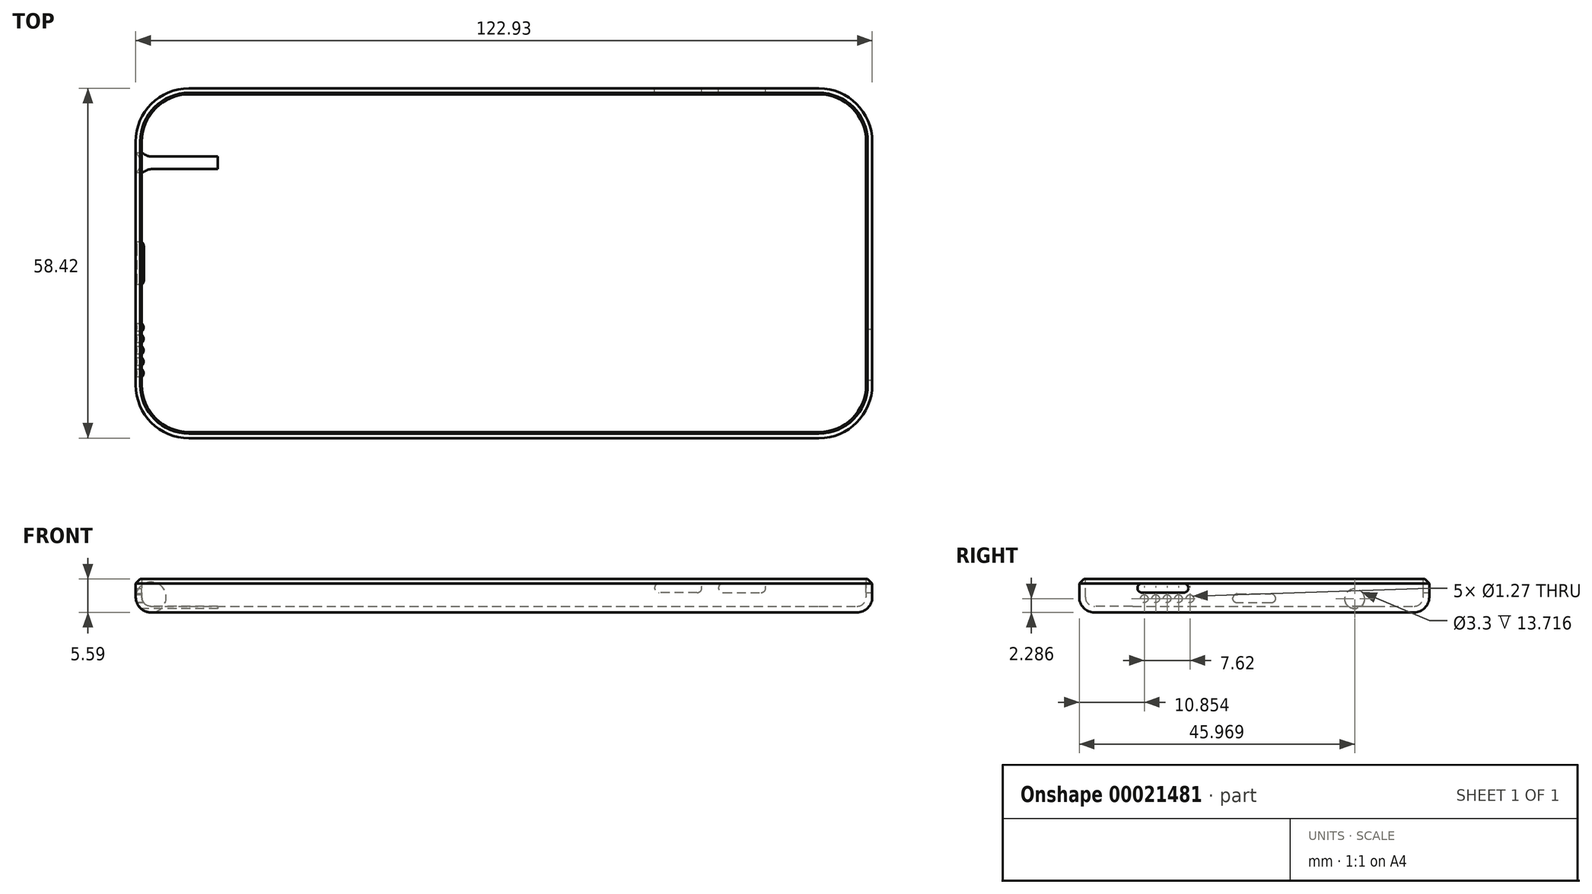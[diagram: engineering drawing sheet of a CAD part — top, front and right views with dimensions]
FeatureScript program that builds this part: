
annotation { "Feature Type Name" : "Feature", "Feature Type Description" : "" }
export const myFeature = defineFeature(function(context is Context, id is Id, definition is map)
    precondition{}
    {
        {
            var Q0;
            Q0=qCreatedBy(makeId("Top.planeOp"),FACE);
            var sketch = newSketch(context, id + "F0", { "sketchPlane" : qUnion([Q0])});
            skLineSegment(sketch, "E0.bottom", {"start": v(-46.61, 26.92) * mm, "end": v(58.54, 26.92) * mm});
            skLineSegment(sketch, "E0.top", {"start": v(-46.61, -31.5) * mm, "end": v(58.54, -31.5) * mm});
            skLineSegment(sketch, "E0.left", {"start": v(-55.5, 18.03) * mm, "end": v(-55.5, -22.61) * mm});
            skLineSegment(sketch, "E0.right", {"start": v(67.43, 18.03) * mm, "end": v(67.43, -22.61) * mm});
            skPoint(sketch, "E1.visualSharp", {"position": v(-55.5, 26.92) * mm});
            skArc(sketch, "E1.filletArc", {"start": v(-46.61, 26.92) * mm, "mid": v(-52.9, 24.31) * mm, "end": v(-55.5, 18.03) * mm});
            skPoint(sketch, "E2.visualSharp", {"position": v(67.43, 26.92) * mm});
            skArc(sketch, "E2.filletArc", {"start": v(67.43, 18.03) * mm, "mid": v(64.83, 24.31) * mm, "end": v(58.54, 26.92) * mm});
            skPoint(sketch, "E3.visualSharp", {"position": v(67.43, -31.5) * mm});
            skArc(sketch, "E3.filletArc", {"start": v(58.54, -31.5) * mm, "mid": v(64.83, -28.9) * mm, "end": v(67.43, -22.61) * mm});
            skPoint(sketch, "E4.visualSharp", {"position": v(-55.5, -31.5) * mm});
            skArc(sketch, "E4.filletArc", {"start": v(-55.5, -22.61) * mm, "mid": v(-52.9, -28.9) * mm, "end": v(-46.61, -31.5) * mm});
            skSolve(sketch);
        }
        {
            var Q0;
            Q0=makeQuery(id+"F0.imprint","IMPRINT",FACE,{"disambiguationData":[TD([[makeQuery(id+"F0.imprint","IMPRINT",EDGE,{"derivedFrom":sQuery(id+"F0.wireOp",EDGE,"E0.bottom")}),-1.0]])]});
            extrude(context, id + "F1", {"entities" : qUnion([Q0]), "depth" : 5.6 * mm});
        }
        {
            var Q0;
            Q0=makeQuery(id+"F1.opExtrude","SWEPT_FACE",FACE,{"disambiguationData":[OSD([sQuery(id+"F0.wireOp",EDGE,"E0.right")])]});
            var sketch = newSketch(context, id + "F2", { "sketchPlane" : qUnion([Q0])});
            skLineSegment(sketch, "E5", {"start": v(-14.04, 3.3) * mm, "end": v(-21.03, 3.3) * mm});
            skArc(sketch, "E6", {"start": v(-21.03, 4.83) * mm, "mid": v(-21.79, 4.06) * mm, "end": v(-21.03, 3.3) * mm});
            skArc(sketch, "E7", {"start": v(-14.04, 3.3) * mm, "mid": v(-13.28, 4.06) * mm, "end": v(-14.04, 4.83) * mm});
            skLineSegment(sketch, "E8", {"start": v(-14.04, 4.83) * mm, "end": v(-21.03, 4.83) * mm});
            skSolve(sketch);
        }
        {
            var Q0;
            Q0=makeQuery(id+"F1.opExtrude","SWEPT_FACE",FACE,{"disambiguationData":[OSD([sQuery(id+"F0.wireOp",EDGE,"E0.bottom")])]});
            var sketch = newSketch(context, id + "F3", { "sketchPlane" : qUnion([Q0])});
            skLineSegment(sketch, "E9", {"start": v(-42.54, 3.3) * mm, "end": v(-48.9, 3.3) * mm});
            skLineSegment(sketch, "E10", {"start": v(-49.65, 4.06) * mm, "end": v(-49.65, 4.06) * mm});
            skLineSegment(sketch, "E11", {"start": v(-48.9, 4.83) * mm, "end": v(-42.54, 4.83) * mm});
            skLineSegment(sketch, "E12", {"start": v(-41.78, 4.06) * mm, "end": v(-41.78, 4.06) * mm});
            skLineSegment(sketch, "E13", {"start": v(-38.98, 4.06) * mm, "end": v(-38.98, 4.06) * mm});
            skLineSegment(sketch, "E14", {"start": v(-38.22, 3.3) * mm, "end": v(-31.87, 3.3) * mm});
            skLineSegment(sketch, "E15", {"start": v(-31.11, 4.06) * mm, "end": v(-31.11, 4.06) * mm});
            skLineSegment(sketch, "E16", {"start": v(-31.87, 4.83) * mm, "end": v(-38.22, 4.83) * mm});
            skArc(sketch, "E17.filletArc", {"start": v(-48.9, 4.83) * mm, "mid": v(-49.43, 4.6) * mm, "end": v(-49.65, 4.06) * mm});
            skArc(sketch, "E18.filletArc", {"start": v(-49.65, 4.06) * mm, "mid": v(-49.43, 3.53) * mm, "end": v(-48.9, 3.3) * mm});
            skArc(sketch, "E19.filletArc", {"start": v(-42.54, 3.3) * mm, "mid": v(-42, 3.53) * mm, "end": v(-41.78, 4.06) * mm});
            skArc(sketch, "E20.filletArc", {"start": v(-41.78, 4.06) * mm, "mid": v(-42, 4.6) * mm, "end": v(-42.54, 4.83) * mm});
            skArc(sketch, "E21.filletArc", {"start": v(-38.22, 4.83) * mm, "mid": v(-38.76, 4.6) * mm, "end": v(-38.98, 4.06) * mm});
            skArc(sketch, "E22.filletArc", {"start": v(-38.98, 4.06) * mm, "mid": v(-38.76, 3.53) * mm, "end": v(-38.22, 3.3) * mm});
            skArc(sketch, "E23.filletArc", {"start": v(-31.11, 4.06) * mm, "mid": v(-31.33, 4.6) * mm, "end": v(-31.87, 4.83) * mm});
            skArc(sketch, "E24.filletArc", {"start": v(-31.87, 3.3) * mm, "mid": v(-31.33, 3.53) * mm, "end": v(-31.11, 4.06) * mm});
            skSolve(sketch);
        }
        {
            var Q0;
            Q0=makeQuery(id+"F1.opExtrude","SWEPT_FACE",FACE,{"disambiguationData":[OSD([sQuery(id+"F0.wireOp",EDGE,"E0.left")])]});
            var sketch = newSketch(context, id + "F4", { "sketchPlane" : qUnion([Q0])});
            skCircle(sketch, "E25", {"center": v(-14.47, 2.29) * mm, "radius": 1.65 * mm});
            skCircle(sketch, "E26", {"center": v(20.65, 2.29) * mm, "radius": 0.64 * mm});
            skCircle(sketch, "E27", {"center": v(18.74, 2.29) * mm, "radius": 0.64 * mm});
            skCircle(sketch, "E28", {"center": v(16.84, 2.29) * mm, "radius": 0.64 * mm});
            skCircle(sketch, "E29", {"center": v(14.93, 2.29) * mm, "radius": 0.64 * mm});
            skCircle(sketch, "E30", {"center": v(13.03, 2.29) * mm, "radius": 0.64 * mm});
            skLineSegment(sketch, "E31", {"start": v(-0.49, 1.57) * mm, "end": v(5.1, 1.57) * mm});
            skLineSegment(sketch, "E32", {"start": v(5.1, 3.1) * mm, "end": v(-0.49, 3.1) * mm});
            skLineSegment(sketch, "E33", {"start": v(-1.25, 2.34) * mm, "end": v(-1.25, 2.34) * mm});
            skLineSegment(sketch, "E34", {"start": v(5.86, 2.34) * mm, "end": v(5.86, 2.34) * mm});
            skArc(sketch, "E35.filletArc", {"start": v(5.86, 2.34) * mm, "mid": v(5.64, 2.87) * mm, "end": v(5.1, 3.1) * mm});
            skArc(sketch, "E36.filletArc", {"start": v(5.1, 1.57) * mm, "mid": v(5.64, 1.8) * mm, "end": v(5.86, 2.34) * mm});
            skArc(sketch, "E37.filletArc", {"start": v(-1.25, 2.34) * mm, "mid": v(-1.03, 1.8) * mm, "end": v(-0.49, 1.57) * mm});
            skArc(sketch, "E38.filletArc", {"start": v(-0.49, 3.1) * mm, "mid": v(-1.03, 2.87) * mm, "end": v(-1.25, 2.34) * mm});
            skLineSegment(sketch, "E39", {"start": v(5.85, 2.34) * mm, "end": v(5.86, 2.34) * mm});
            skSolve(sketch);
        }
        {
            var Q0;
            Q0=makeQuery(id+"F1.opExtrude","CAP_EDGE",EDGE,{"disambiguationData":[OSD([sQuery(id+"F0.wireOp",EDGE,"E0.left")])],"isStart":true});
            var Q1;
            Q1=makeQuery(id+"F1.opExtrude","CAP_EDGE",EDGE,{"disambiguationData":[OSD([sQuery(id+"F0.wireOp",EDGE,"E1.filletArc")])],"isStart":true});
            var Q2;
            Q2=makeQuery(id+"F1.opExtrude","CAP_EDGE",EDGE,{"disambiguationData":[OSD([sQuery(id+"F0.wireOp",EDGE,"E4.filletArc")])],"isStart":true});
            var Q3;
            Q3=makeQuery(id+"F1.opExtrude","CAP_EDGE",EDGE,{"disambiguationData":[OSD([sQuery(id+"F0.wireOp",EDGE,"E0.top")])],"isStart":true});
            var Q4;
            Q4=makeQuery(id+"F1.opExtrude","CAP_EDGE",EDGE,{"disambiguationData":[OSD([sQuery(id+"F0.wireOp",EDGE,"E0.bottom")])],"isStart":true});
            var Q5;
            Q5=makeQuery(id+"F1.opExtrude","CAP_EDGE",EDGE,{"disambiguationData":[OSD([sQuery(id+"F0.wireOp",EDGE,"E2.filletArc")])],"isStart":true});
            var Q6;
            Q6=makeQuery(id+"F1.opExtrude","CAP_EDGE",EDGE,{"disambiguationData":[OSD([sQuery(id+"F0.wireOp",EDGE,"E0.right")])],"isStart":true});
            var Q7;
            Q7=makeQuery(id+"F1.opExtrude","CAP_EDGE",EDGE,{"disambiguationData":[OSD([sQuery(id+"F0.wireOp",EDGE,"E3.filletArc")])],"isStart":true});
            fillet(context, id + "F5", {"entities" : qUnion([Q0, Q1, Q2, Q3, Q4, Q5, Q6, Q7]), "radius" : 2.54 * mm, "tangentPropagation" : true, "allowEdgeOverflow" : false});
        }
        {
            var Q0;
            Q0=makeQuery(id+"F1.opExtrude","CAP_FACE",FACE,{"disambiguationData":[OSD([sQuery(id+"F0.wireOp",EDGE,"E0.bottom"),sQuery(id+"F0.wireOp",EDGE,"E0.top"),sQuery(id+"F0.wireOp",EDGE,"E0.left"),sQuery(id+"F0.wireOp",EDGE,"E0.right"),sQuery(id+"F0.wireOp",EDGE,"E1.filletArc"),sQuery(id+"F0.wireOp",EDGE,"E2.filletArc"),sQuery(id+"F0.wireOp",EDGE,"E3.filletArc"),sQuery(id+"F0.wireOp",EDGE,"E4.filletArc")])],"isStart":false});
            shell(context, id + "F6", {"entities" : qUnion([Q0]), "thickness" : 1.02 * mm});
        }
        {
            var Q0;
            Q0=makeQuery(id+"F2.imprint","IMPRINT",FACE,{"disambiguationData":[TD([[makeQuery(id+"F2.imprint","IMPRINT",EDGE,{"derivedFrom":sQuery(id+"F2.wireOp",EDGE,"E5")}),-1.0]])]});
            extrude(context, id + "F7", {"entities" : qUnion([Q0]), "operationType" : NewBodyOperationType.REMOVE, "oppositeDirection" : true, "depth" : 1.02 * mm});
        }
        {
            var Q0;
            Q0=makeQuery(id+"F3.imprint","IMPRINT",FACE,{"disambiguationData":[TD([[makeQuery(id+"F3.imprint","IMPRINT",EDGE,{"derivedFrom":sQuery(id+"F3.wireOp",EDGE,"E9")}),-1.0]])]});
            var Q1;
            Q1=makeQuery(id+"F3.imprint","IMPRINT",FACE,{"disambiguationData":[TD([[makeQuery(id+"F3.imprint","IMPRINT",EDGE,{"derivedFrom":sQuery(id+"F3.wireOp",EDGE,"E14")}),1.0]])]});
            extrude(context, id + "F8", {"entities" : qUnion([Q0, Q1]), "operationType" : NewBodyOperationType.REMOVE, "oppositeDirection" : true, "depth" : 1.02 * mm});
        }
        {
            var Q0;
            Q0=makeQuery(id+"F4.imprint","IMPRINT",FACE,{"disambiguationData":[TD([[makeQuery(id+"F4.imprint","IMPRINT",EDGE,{"derivedFrom":sQuery(id+"F4.wireOp",EDGE,"E25")}),1.0]])]});
            var Q1;
            Q1=makeQuery(id+"F4.imprint","IMPRINT",FACE,{"disambiguationData":[TD([[makeQuery(id+"F4.imprint","IMPRINT",EDGE,{"derivedFrom":sQuery(id+"F4.wireOp",EDGE,"E31")}),1.0]])]});
            var Q2;
            Q2=makeQuery(id+"F4.imprint","IMPRINT",FACE,{"disambiguationData":[TD([[makeQuery(id+"F4.imprint","IMPRINT",EDGE,{"derivedFrom":sQuery(id+"F4.wireOp",EDGE,"E30")}),1.0]])]});
            var Q3;
            Q3=makeQuery(id+"F4.imprint","IMPRINT",FACE,{"disambiguationData":[TD([[makeQuery(id+"F4.imprint","IMPRINT",EDGE,{"derivedFrom":sQuery(id+"F4.wireOp",EDGE,"E29")}),1.0]])]});
            var Q4;
            Q4=makeQuery(id+"F4.imprint","IMPRINT",FACE,{"disambiguationData":[TD([[makeQuery(id+"F4.imprint","IMPRINT",EDGE,{"derivedFrom":sQuery(id+"F4.wireOp",EDGE,"E28")}),1.0]])]});
            var Q5;
            Q5=makeQuery(id+"F4.imprint","IMPRINT",FACE,{"disambiguationData":[TD([[makeQuery(id+"F4.imprint","IMPRINT",EDGE,{"derivedFrom":sQuery(id+"F4.wireOp",EDGE,"E26")}),1.0]])]});
            var Q6;
            Q6=makeQuery(id+"F4.imprint","IMPRINT",FACE,{"disambiguationData":[TD([[makeQuery(id+"F4.imprint","IMPRINT",EDGE,{"derivedFrom":sQuery(id+"F4.wireOp",EDGE,"E27")}),1.0]])]});
            extrude(context, id + "F9", {"entities" : qUnion([Q0, Q1, Q2, Q3, Q4, Q5, Q6]), "operationType" : NewBodyOperationType.REMOVE, "oppositeDirection" : true, "depth" : 1.02 * mm});
        }
        {
            var Q0;
            Q0=makeQuery(id+"F9.boolean.opBoolean","COPY",FACE,{"derivedFrom":makeQuery(id+"F9.opExtrude","CAP_FACE",FACE,{"disambiguationData":[OSD([sQuery(id+"F4.wireOp",EDGE,"E30")])],"isStart":false})});
            extrude(context, id + "F10", {"entities" : qUnion([Q0]), "operationType" : NewBodyOperationType.REMOVE, "oppositeDirection" : true, "depth" : 25.4 * mm});
        }
        {
            var Q0;
            Q0=makeQuery(id+"F9.boolean.opBoolean","COPY",FACE,{"derivedFrom":makeQuery(id+"F9.opExtrude","CAP_FACE",FACE,{"disambiguationData":[OSD([sQuery(id+"F4.wireOp",EDGE,"E29")])],"isStart":false})});
            extrude(context, id + "F11", {"entities" : qUnion([Q0]), "operationType" : NewBodyOperationType.REMOVE, "oppositeDirection" : true, "depth" : 25.4 * mm});
        }
        {
            var Q0;
            Q0=makeQuery(id+"F9.boolean.opBoolean","COPY",FACE,{"derivedFrom":makeQuery(id+"F9.opExtrude","CAP_FACE",FACE,{"disambiguationData":[OSD([sQuery(id+"F4.wireOp",EDGE,"E28")])],"isStart":false})});
            extrude(context, id + "F12", {"entities" : qUnion([Q0]), "operationType" : NewBodyOperationType.REMOVE, "oppositeDirection" : true, "depth" : 25.4 * mm});
        }
        {
            var Q0;
            Q0=makeQuery(id+"F9.boolean.opBoolean","COPY",FACE,{"derivedFrom":makeQuery(id+"F9.opExtrude","CAP_FACE",FACE,{"disambiguationData":[OSD([sQuery(id+"F4.wireOp",EDGE,"E27")])],"isStart":false})});
            var Q1;
            Q1=makeQuery(id+"F9.boolean.opBoolean","COPY",FACE,{"derivedFrom":makeQuery(id+"F9.opExtrude","CAP_FACE",FACE,{"disambiguationData":[OSD([sQuery(id+"F4.wireOp",EDGE,"E26")])],"isStart":false})});
            var Q2;
            Q2=makeQuery(id+"F9.boolean.opBoolean","COPY",FACE,{"derivedFrom":makeQuery(id+"F9.opExtrude","CAP_FACE",FACE,{"disambiguationData":[OSD([sQuery(id+"F4.wireOp",EDGE,"E31"),sQuery(id+"F4.wireOp",EDGE,"E32"),sQuery(id+"F4.wireOp",EDGE,"E35.filletArc"),sQuery(id+"F4.wireOp",EDGE,"E36.filletArc"),sQuery(id+"F4.wireOp",EDGE,"E37.filletArc"),sQuery(id+"F4.wireOp",EDGE,"E38.filletArc")])],"isStart":false})});
            var Q3;
            Q3=makeQuery(id+"F9.boolean.opBoolean","COPY",FACE,{"derivedFrom":makeQuery(id+"F9.opExtrude","CAP_FACE",FACE,{"disambiguationData":[OSD([sQuery(id+"F4.wireOp",EDGE,"E25")])],"isStart":false})});
            extrude(context, id + "F13", {"entities" : qUnion([Q0, Q1, Q2, Q3]), "operationType" : NewBodyOperationType.REMOVE, "oppositeDirection" : true, "depth" : 12.7 * mm});
        }
        {
            var Q0;
            Q0=makeQuery(id+"F1.opExtrude","CAP_EDGE",EDGE,{"disambiguationData":[OSD([sQuery(id+"F0.wireOp",EDGE,"E0.top")])],"isStart":false});
            var Q1;
            Q1=makeQuery(id+"F1.opExtrude","CAP_EDGE",EDGE,{"disambiguationData":[OSD([sQuery(id+"F0.wireOp",EDGE,"E4.filletArc")])],"isStart":false});
            var Q2;
            Q2=makeQuery(id+"F1.opExtrude","CAP_EDGE",EDGE,{"disambiguationData":[OSD([sQuery(id+"F0.wireOp",EDGE,"E0.left")])],"isStart":false});
            var Q3;
            Q3=makeQuery(id+"F1.opExtrude","CAP_EDGE",EDGE,{"disambiguationData":[OSD([sQuery(id+"F0.wireOp",EDGE,"E1.filletArc")])],"isStart":false});
            var Q4;
            Q4=makeQuery(id+"F1.opExtrude","CAP_EDGE",EDGE,{"disambiguationData":[OSD([sQuery(id+"F0.wireOp",EDGE,"E0.bottom")])],"isStart":false});
            var Q5;
            Q5=makeQuery(id+"F1.opExtrude","CAP_EDGE",EDGE,{"disambiguationData":[OSD([sQuery(id+"F0.wireOp",EDGE,"E2.filletArc")])],"isStart":false});
            var Q6;
            Q6=makeQuery(id+"F1.opExtrude","CAP_EDGE",EDGE,{"disambiguationData":[OSD([sQuery(id+"F0.wireOp",EDGE,"E0.right")])],"isStart":false});
            var Q7;
            Q7=makeQuery(id+"F1.opExtrude","CAP_EDGE",EDGE,{"disambiguationData":[OSD([sQuery(id+"F0.wireOp",EDGE,"E3.filletArc")])],"isStart":false});
            chamfer(context, id + "F14", {"entities" : qUnion([Q0, Q1, Q2, Q3, Q4, Q5, Q6, Q7]), "width" : 0.76 * mm, "tangentPropagation" : true});
        }
    });
